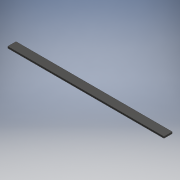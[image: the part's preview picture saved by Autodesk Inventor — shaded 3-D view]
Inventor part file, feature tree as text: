
AUTODESK INVENTOR PART (.ipt)
format: ipt  version: 2018 (Build 220112000, 112)  size: 94,720 bytes
history: native  units: mm
features: extrude x1, sketch x1
ambient origin geometry x8: Origin, YZ Plane, XZ Plane, XY Plane, X Axis, Y Axis, Z Axis, Center Point
bodies: Solid1 (feature_tree)
feature tree (2):
  extrude  "Extrusion1"  Depth=10.0mm
  sketch  "Sketch1"  dims[d0=190.0mm d1=10.0mm d2=2.0mm d3=0.0mm]
